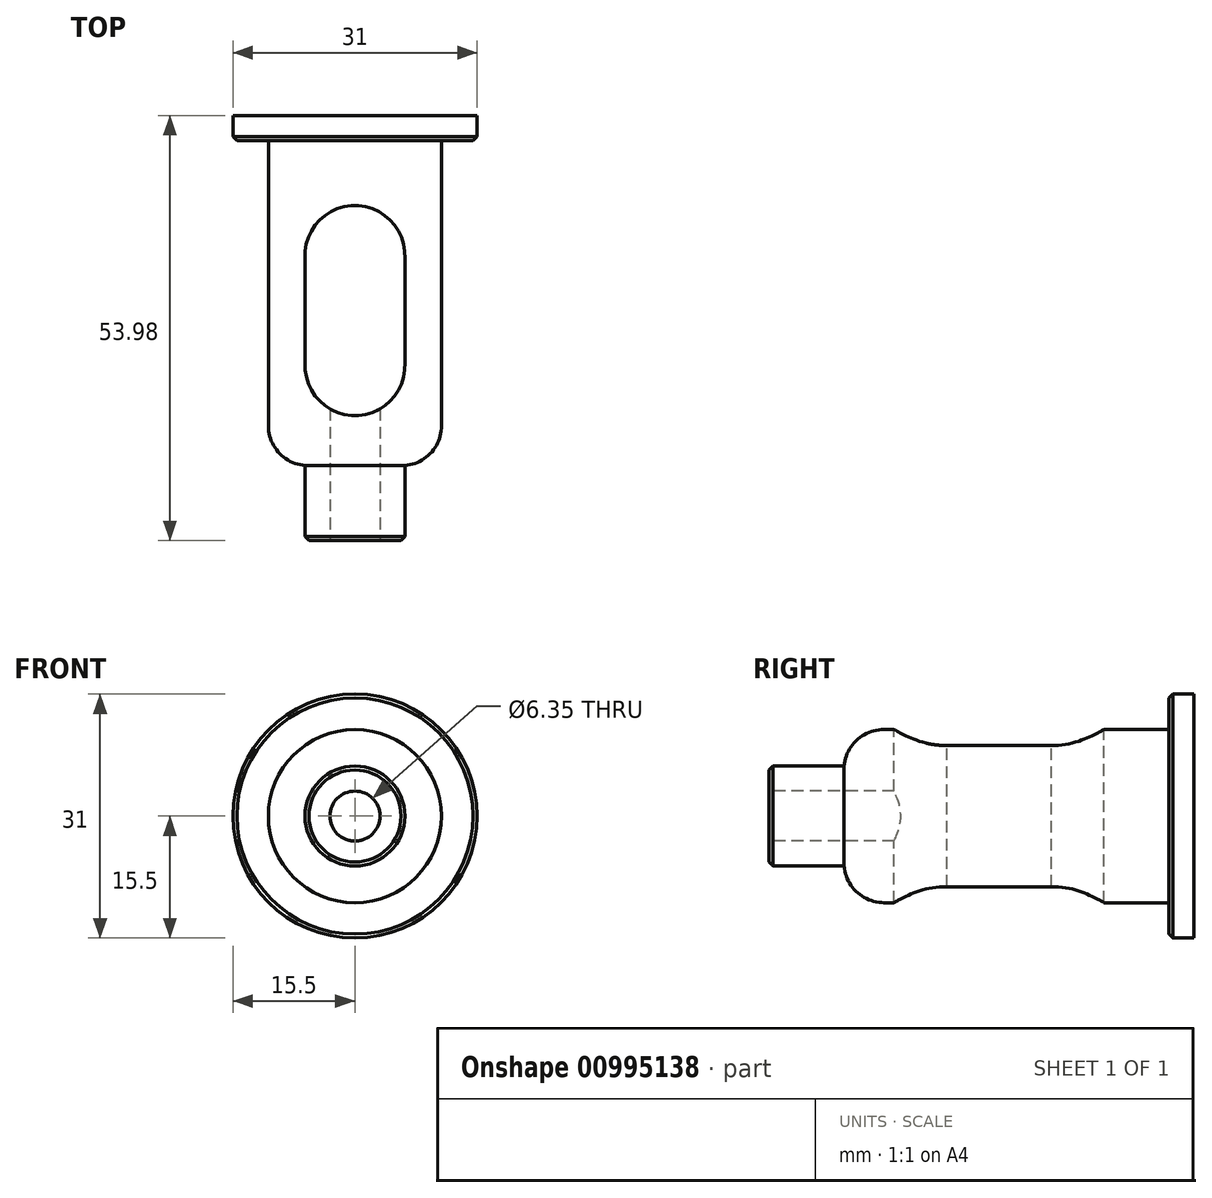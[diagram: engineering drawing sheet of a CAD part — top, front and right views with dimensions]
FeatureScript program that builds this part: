
annotation { "Feature Type Name" : "Feature", "Feature Type Description" : "" }
export const myFeature = defineFeature(function(context is Context, id is Id, definition is map)
    precondition{}
    {
        {
            var Q0;
            Q0=qCreatedBy(makeId("Front.planeOp"),FACE);
            var sketch = newSketch(context, id + "F0", { "sketchPlane" : qUnion([Q0])});
            skCircle(sketch, "E0", {"center": v(0, 0) * mm, "radius": 11 * mm});
            skCircle(sketch, "E1", {"center": v(0, 0) * mm, "radius": 15.5 * mm});
            skSolve(sketch);
        }
        {
            var Q0;
            Q0=makeQuery(id+"F0.imprint","IMPRINT",FACE,{"disambiguationData":[TD([[makeQuery(id+"F0.imprint","IMPRINT",EDGE,{"derivedFrom":sQuery(id+"F0.wireOp",EDGE,"E0")}),1.0]])]});
            extrude(context, id + "F1", {"entities" : qUnion([Q0]), "flatOperationType" : FlatOperationType.REMOVE, "depth" : 44.45 * mm, "offsetDistance" : 25.4 * mm, "domain" : OperationDomain.MODEL});
        }
        {
            var Q0;
            Q0=makeQuery(id+"F0.imprint","IMPRINT",FACE,{"disambiguationData":[TD([[makeQuery(id+"F0.imprint","IMPRINT",EDGE,{"derivedFrom":sQuery(id+"F0.wireOp",EDGE,"E0")}),-1.0]])]});
            extrude(context, id + "F2", {"entities" : qUnion([Q0]), "operationType" : NewBodyOperationType.ADD, "depth" : 3.17 * mm, "offsetDistance" : 25.4 * mm});
        }
        {
            var Q0;
            Q0=makeQuery(id+"F1.opExtrude","CAP_FACE",FACE,{"disambiguationData":[OSD([sQuery(id+"F0.wireOp",EDGE,"E0")])],"isStart":false});
            var sketch = newSketch(context, id + "F3", { "sketchPlane" : qUnion([Q0])});
            skCircle(sketch, "E2", {"center": v(0, 0) * mm, "radius": 6.35 * mm});
            skSolve(sketch);
        }
        {
            var Q0;
            Q0=makeQuery(id+"F3.imprint","IMPRINT",FACE,{"disambiguationData":[TD([[makeQuery(id+"F3.imprint","IMPRINT",EDGE,{"derivedFrom":sQuery(id+"F3.wireOp",EDGE,"E2")}),1.0]])]});
            extrude(context, id + "F4", {"entities" : qUnion([Q0]), "operationType" : NewBodyOperationType.ADD, "depth" : 9.52 * mm, "offsetDistance" : 25.4 * mm});
        }
        {
            var Q0;
            Q0=makeQuery(id+"F1.opExtrude","CAP_EDGE",EDGE,{"disambiguationData":[OSD([sQuery(id+"F0.wireOp",EDGE,"E0")])],"isStart":false});
            fillet(context, id + "F5", {"entities" : qUnion([Q0]), "radius" : 5.08 * mm, "tangentPropagation" : true, "allowEdgeOverflow" : false});
        }
        {
            var Q0;
            Q0=qCreatedBy(makeId("Top.planeOp"),FACE);
            var sketch = newSketch(context, id + "F6", { "sketchPlane" : qUnion([Q0])});
            skLineSegment(sketch, "E3", {"start": v(0, 0) * mm, "end": v(0, -17.78) * mm, "construction": true});
            skLineSegment(sketch, "E4", {"start": v(0, -17.78) * mm, "end": v(0, -31.75) * mm, "construction": true});
            skArc(sketch, "E5", {"start": v(-6.34, -31.4) * mm, "mid": v(0, -38.1) * mm, "end": v(6.34, -31.4) * mm});
            skArc(sketch, "E6", {"start": v(6.34, -18.14) * mm, "mid": v(0, -11.43) * mm, "end": v(-6.34, -18.14) * mm});
            skLineSegment(sketch, "E7", {"start": v(-6.34, -17.42) * mm, "end": v(-6.34, -32.1) * mm});
            skLineSegment(sketch, "E8.MirrorCS", {"start": v(6.34, -17.42) * mm, "end": v(6.34, -32.1) * mm});
            skSolve(sketch);
        }
        {
            var Q0;
            Q0 = qSketchRegion(id + "F6", true);
            extrude(context, id + "F7", {"entities" : qUnion([Q0]), "operationType" : NewBodyOperationType.REMOVE, "oppositeDirection" : true, "depth" : 25.4 * mm, "offsetDistance" : 25.4 * mm, "hasSecondDirection" : true, "secondDirectionOppositeDirection" : false, "secondDirectionDepth" : 25.4 * mm});
        }
        {
            var Q0;
            Q0=makeQuery(id+"F4.opExtrude","CAP_FACE",FACE,{"disambiguationData":[OSD([sQuery(id+"F3.wireOp",EDGE,"E2")])],"isStart":false});
            var sketch = newSketch(context, id + "F8", { "sketchPlane" : qUnion([Q0])});
            skCircle(sketch, "E9", {"center": v(0, 0) * mm, "radius": 3.18 * mm});
            skSolve(sketch);
        }
        {
            var Q0;
            Q0 = qSketchRegion(id + "F8", true);
            extrude(context, id + "F9", {"entities" : qUnion([Q0]), "operationType" : NewBodyOperationType.REMOVE, "oppositeDirection" : true, "depth" : 25.4 * mm, "offsetDistance" : 25.4 * mm});
        }
        {
            var Q0;
            Q0=makeQuery(id+"F2.opExtrude","CAP_EDGE",EDGE,{"disambiguationData":[OSD([sQuery(id+"F0.wireOp",EDGE,"E1")])],"isStart":false});
            var Q1;
            Q1=makeQuery(id+"F4.opExtrude","CAP_EDGE",EDGE,{"disambiguationData":[OSD([sQuery(id+"F3.wireOp",EDGE,"E2")])],"isStart":false});
            chamfer(context, id + "F10", {"entities" : qUnion([Q0, Q1]), "width" : 0.5 * mm, "tangentPropagation" : true});
        }
    });
